FCSTD DOCUMENT  (FreeCAD 1.0R39109 (Git))
Label: TB-Hotel
License: All rights reserved
LicenseURL: https://en.wikipedia.org/wiki/All_rights_reserved
objects: Spreadsheet::Sheet×1, Sketcher::SketchObject×1, PartDesign::Body×1
note: 3 computed .brp shape members not serialized (recipe doc carries the construction recipe); baked Part::Feature solids carry a one-line shape summary decoded from their .brp

FEATURE [Spreadsheet::Sheet] Spreadsheet  label="Measurement"
  cells = A1='box_width; B1(box_width)==10 mm; A2='box_height; B2(box_height)==6 mm
FEATURE [Sketcher::SketchObject] Sketch
  ArcFitTolerance = 1e-06
  AttachmentSupport = -> [XY_Plane]
  FullyConstrained = true
  MakeInternals = false
  MapMode = 5
  expr: Constraints[10] = Spreadsheet.box_width
  expr: Constraints[11] = Spreadsheet.box_height
  sketch-geometry (5):
    g0: LineSegment StartX=5 StartY=-3 StartZ=0 EndX=5 EndY=3 EndZ=0
    g1: LineSegment StartX=5 StartY=3 StartZ=0 EndX=-5 EndY=3 EndZ=0
    g2: LineSegment StartX=-5 StartY=3 StartZ=0 EndX=-5 EndY=-3 EndZ=0
    g3: LineSegment StartX=-5 StartY=-3 StartZ=0 EndX=5 EndY=-3 EndZ=0
    g4: GeomPoint [constr] X=0 Y=0 Z=0
  constraints (12):
    c: Coincident(g0,g1)
    c: Coincident(g1,g2)
    c: Coincident(g2,g3)
    c: Coincident(g3,g0)
    c: Vertical(g0)
    c: Vertical(g2)
    c: Horizontal(g1)
    c: Horizontal(g3)
    c: Symmetric(g2,g0,g4)
    c: Coincident(g4,g-1)
    c: DistanceX(g1,g1) = 10
    c: DistanceY(g2,g2) = 6
FEATURE [PartDesign::Body] Body
  AllowCompound = false
  Group = -> [Sketch]
  Origin = -> Origin
